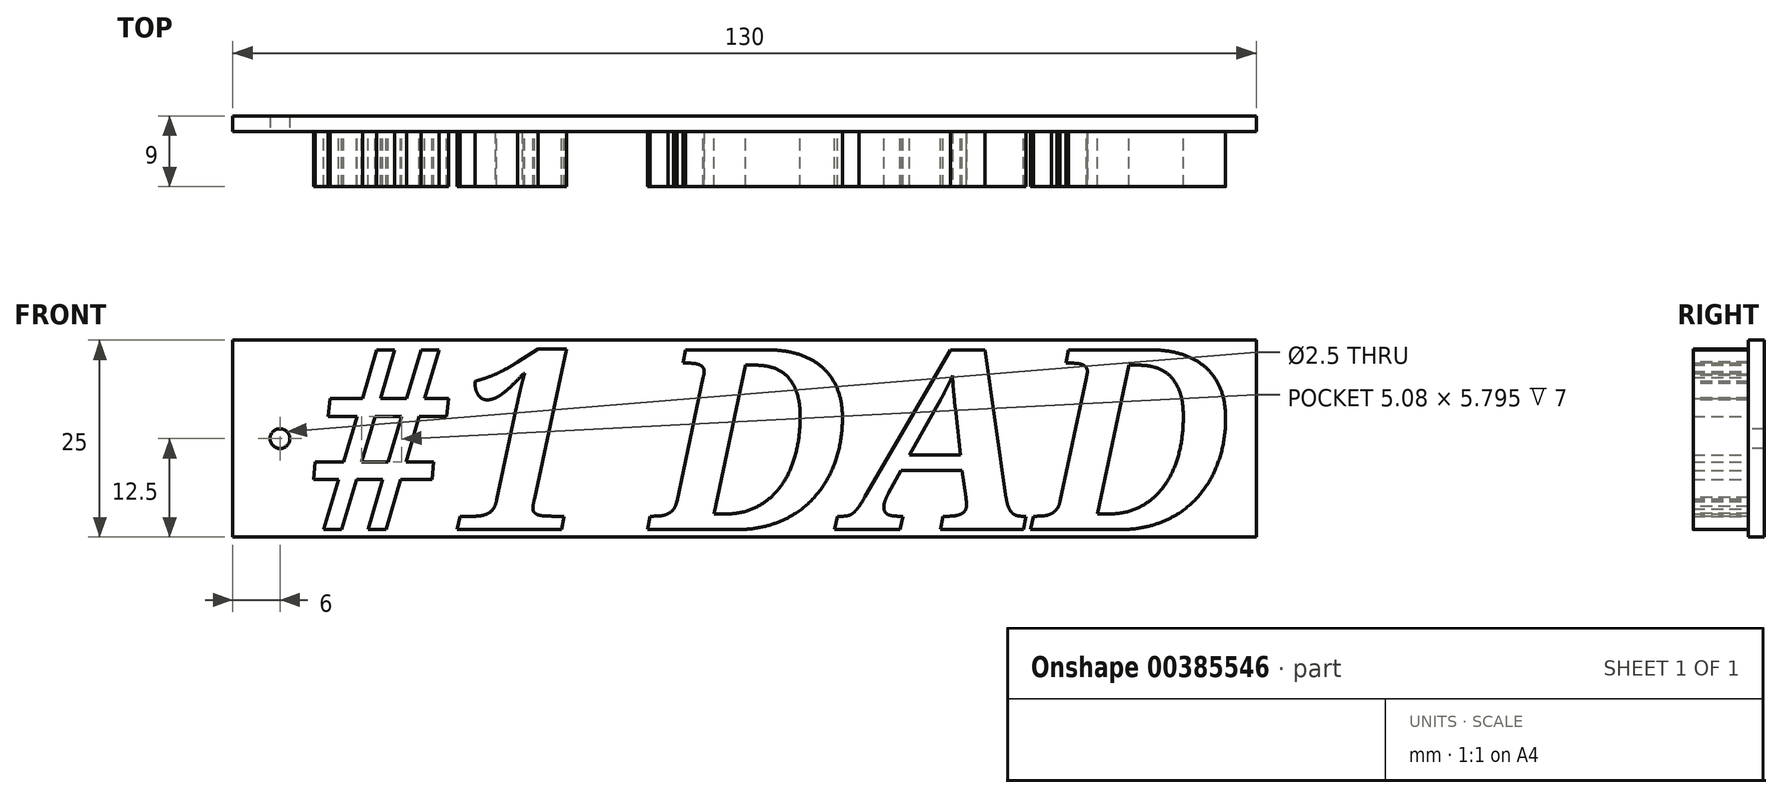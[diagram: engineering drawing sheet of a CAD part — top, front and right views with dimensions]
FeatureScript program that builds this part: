
annotation { "Feature Type Name" : "Feature", "Feature Type Description" : "" }
export const myFeature = defineFeature(function(context is Context, id is Id, definition is map)
    precondition{}
    {
        {
            var Q0;
            Q0=qCreatedBy(makeId("Front.planeOp"),FACE);
            var sketch = newSketch(context, id + "F0", { "sketchPlane" : qUnion([Q0])});
            skLineSegment(sketch, "E0.bottom", {"start": v(65, -12.5) * mm, "end": v(-65, -12.5) * mm});
            skLineSegment(sketch, "E0.top", {"start": v(65, 12.5) * mm, "end": v(-65, 12.5) * mm});
            skLineSegment(sketch, "E0.left", {"start": v(65, -12.5) * mm, "end": v(65, 12.5) * mm});
            skLineSegment(sketch, "E0.right", {"start": v(-65, -12.5) * mm, "end": v(-65, 12.5) * mm});
            skPoint(sketch, "E0.middle", {"position": v(0, 0) * mm});
            skCircle(sketch, "E1", {"center": v(-59, 0) * mm, "radius": 1.25 * mm});
            skSolve(sketch);
        }
        {
            var Q0;
            Q0=qCreatedBy(makeId("Front.planeOp"),FACE);
            var sketch = newSketch(context, id + "F1", { "sketchPlane" : qUnion([Q0])});
            skText(sketch, "E2", { "text": "#1 DAD", "fontName": "NotoSerif-BoldItalic.ttf"});
            const initialGuessF1  = {"E2": [-0.05565, -0.01156, 1, 0, 0.02304]};
            skSetInitialGuess(sketch, initialGuessF1);
            skSolve(sketch);
        }
        {
            var Q0;
            Q0=makeQuery(id+"F0.imprint","IMPRINT",FACE,{"disambiguationData":[TD([[makeQuery(id+"F0.imprint","IMPRINT",EDGE,{"derivedFrom":sQuery(id+"F0.wireOp",EDGE,"E0.bottom")}),-1.0]])]});
            extrude(context, id + "F2", {"entities" : qUnion([Q0]), "oppositeDirection" : true, "depth" : 2 * mm});
        }
        {
            var Q0;
            Q0 = qSketchRegion(id + "F1", true);
            extrude(context, id + "F3", {"entities" : qUnion([Q0]), "operationType" : NewBodyOperationType.ADD, "depth" : 7 * mm});
        }
    });
